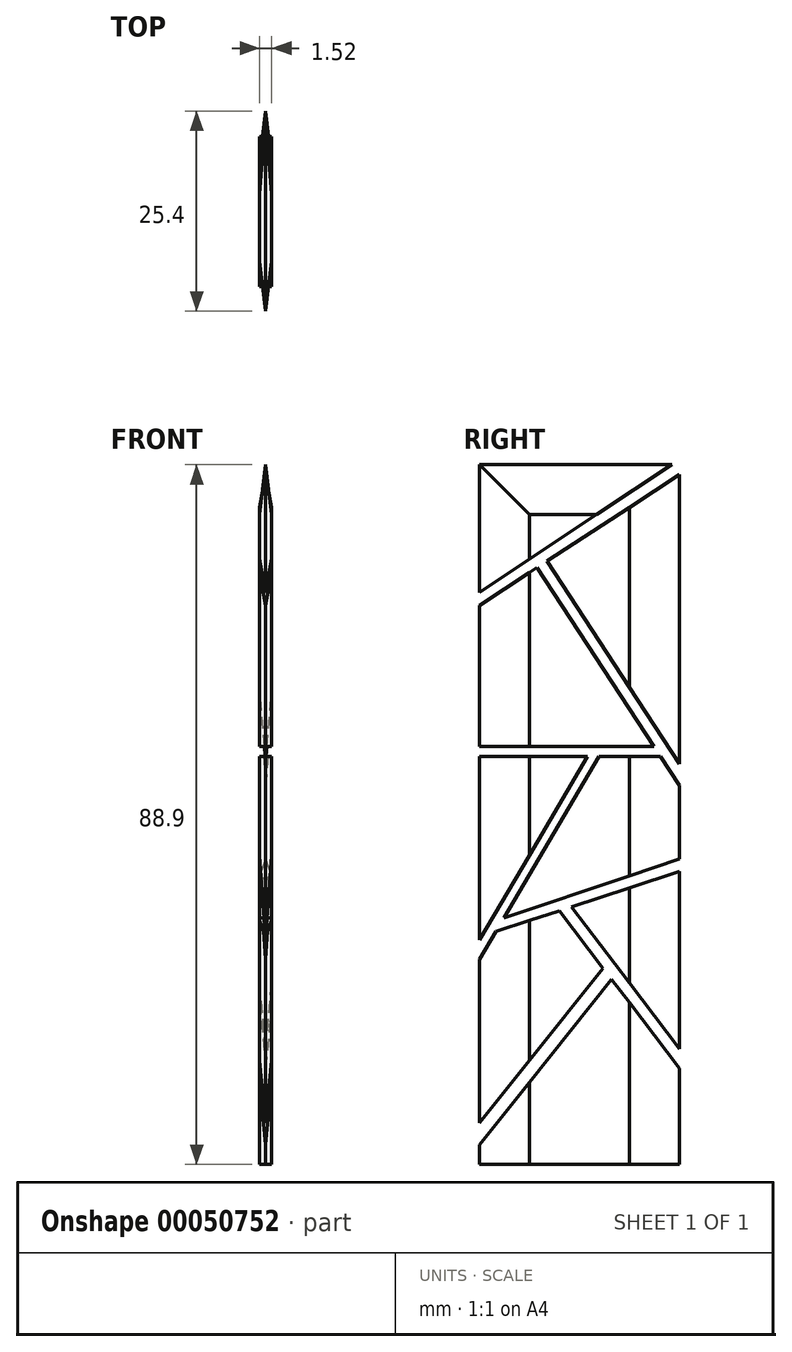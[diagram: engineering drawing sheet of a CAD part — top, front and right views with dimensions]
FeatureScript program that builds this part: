
annotation { "Feature Type Name" : "Feature", "Feature Type Description" : "" }
export const myFeature = defineFeature(function(context is Context, id is Id, definition is map)
    precondition{}
    {
        {
            var Q0;
            Q0=qCreatedBy(makeId("Right.planeOp"),FACE);
            var sketch = newSketch(context, id + "F0", { "sketchPlane" : qUnion([Q0])});
            skLineSegment(sketch, "E0", {"start": v(0, 0) * mm, "end": v(-12.7, 0) * mm});
            skLineSegment(sketch, "E1", {"start": v(-12.7, 0) * mm, "end": v(0, 0) * mm});
            skLineSegment(sketch, "E2", {"start": v(0, 0) * mm, "end": v(12.7, 0) * mm});
            skLineSegment(sketch, "E3", {"start": v(-12.7, 0) * mm, "end": v(-12.7, 51.83) * mm});
            skLineSegment(sketch, "E4", {"start": v(12.7, 0) * mm, "end": v(12.7, 88.9) * mm});
            skLineSegment(sketch, "E5", {"start": v(-12.7, 88.9) * mm, "end": v(11.76, 88.9) * mm});
            skLineSegment(sketch, "E6", {"start": v(11.76, 88.9) * mm, "end": v(-12.7, 72.67) * mm});
            skLineSegment(sketch, "E7", {"start": v(-12.7, 71.03) * mm, "end": v(-5.37, 75.82) * mm});
            skLineSegment(sketch, "E8.trimOffspring", {"start": v(-12.7, 72.67) * mm, "end": v(-12.7, 88.9) * mm});
            skLineSegment(sketch, "E9", {"start": v(-4.12, 76.63) * mm, "end": v(12.7, 50.88) * mm});
            skLineSegment(sketch, "E10", {"start": v(-5.37, 75.82) * mm, "end": v(9.49, 53.08) * mm});
            skLineSegment(sketch, "E11", {"start": v(9.49, 53.08) * mm, "end": v(-12.7, 53.08) * mm});
            skLineSegment(sketch, "E12", {"start": v(-12.7, 51.83) * mm, "end": v(1.05, 51.83) * mm});
            skLineSegment(sketch, "E13.trimOffspring", {"start": v(-12.7, 53.08) * mm, "end": v(-12.7, 71.03) * mm});
            skLineSegment(sketch, "E14.trimOffspring", {"start": v(10.3, 51.83) * mm, "end": v(12.7, 48.17) * mm});
            skLineSegment(sketch, "E15.trimOffspring", {"start": v(-4.12, 76.63) * mm, "end": v(12.7, 87.63) * mm});
            skLineSegment(sketch, "E16", {"start": v(2.51, 51.83) * mm, "end": v(-9.59, 31.31) * mm});
            skLineSegment(sketch, "E17", {"start": v(-12.7, 28.5) * mm, "end": v(1.05, 51.83) * mm});
            skPoint(sketch, "E18.start.orphan", {"position": v(0, 51.83) * mm});
            skLineSegment(sketch, "E19.trimOffspring", {"start": v(2.51, 51.83) * mm, "end": v(10.3, 51.83) * mm});
            skLineSegment(sketch, "E20", {"start": v(-10.6, 29.6) * mm, "end": v(-2.52, 32.23) * mm});
            skLineSegment(sketch, "E21", {"start": v(-9.59, 31.31) * mm, "end": v(12.7, 38.78) * mm});
            skLineSegment(sketch, "E22.trimOffspring", {"start": v(-10.6, 29.6) * mm, "end": v(-12.7, 26.03) * mm});
            skLineSegment(sketch, "E23", {"start": v(-2.52, 32.23) * mm, "end": v(3.03, 24.93) * mm});
            skLineSegment(sketch, "E24", {"start": v(-1.01, 32.73) * mm, "end": v(12.7, 14.67) * mm});
            skPoint(sketch, "E25.start.orphan", {"position": v(0, 33.05) * mm});
            skLineSegment(sketch, "E26", {"start": v(3.03, 24.93) * mm, "end": v(-12.7, 5.26) * mm});
            skLineSegment(sketch, "E27", {"start": v(4.1, 23.51) * mm, "end": v(-12.7, 2.5) * mm});
            skLineSegment(sketch, "E28.trimOffspring", {"start": v(-1.01, 32.73) * mm, "end": v(12.7, 37.2) * mm});
            skLineSegment(sketch, "E29.trimOffspring", {"start": v(4.1, 23.51) * mm, "end": v(12.7, 12.2) * mm});
            skSolve(sketch);
        }
        {
            var Q0;
            Q0 = qSketchRegion(id + "F0", true);
            extrude(context, id + "F1", {"entities" : qUnion([Q0]), "endBound" : BoundingType.SYMMETRIC, "depth" : 1.52 * mm});
        }
        {
            var Q0;
            {var subQ0=sQuery(id+"F0.wireOp",EDGE,"E4");Q0=makeQuery(id+"F1.opExtrude","CAP_EDGE",EDGE,{"disambiguationData":[OSD([subQ0]),TDD([makeQuery(id+"F0.imprint","IMPRINT",EDGE,{"disambiguationData":[TD([[makeQuery(id+"F0.imprint","INTERSECT",VERTEX,{"derivedFrom":[subQ0,sQuery(id+"F0.wireOp",EDGE,"E14.trimOffspring")]}),1.0]])],"derivedFrom":subQ0})])],"isStart":false});}
            var Q1;
            {var subQ0=sQuery(id+"F0.wireOp",EDGE,"E4");Q1=makeQuery(id+"F1.opExtrude","CAP_EDGE",EDGE,{"disambiguationData":[OSD([subQ0]),TDD([makeQuery(id+"F0.imprint","IMPRINT",EDGE,{"disambiguationData":[TD([[makeQuery(id+"F0.imprint","INTERSECT",VERTEX,{"derivedFrom":[subQ0,sQuery(id+"F0.wireOp",EDGE,"E14.trimOffspring")]}),1.0]])],"derivedFrom":subQ0})])],"isStart":true});}
            var Q2;
            {var subQ0=sQuery(id+"F0.wireOp",EDGE,"E4");Q2=makeQuery(id+"F1.opExtrude","CAP_EDGE",EDGE,{"disambiguationData":[OSD([subQ0]),TDD([makeQuery(id+"F0.imprint","IMPRINT",EDGE,{"disambiguationData":[TD([[makeQuery(id+"F0.imprint","INTERSECT",VERTEX,{"derivedFrom":[subQ0,sQuery(id+"F0.wireOp",EDGE,"E9")]}),-1.0]])],"derivedFrom":subQ0})])],"isStart":false});}
            var Q3;
            {var subQ0=sQuery(id+"F0.wireOp",EDGE,"E4");Q3=makeQuery(id+"F1.opExtrude","CAP_EDGE",EDGE,{"disambiguationData":[OSD([subQ0]),TDD([makeQuery(id+"F0.imprint","IMPRINT",EDGE,{"disambiguationData":[TD([[makeQuery(id+"F0.imprint","INTERSECT",VERTEX,{"derivedFrom":[subQ0,sQuery(id+"F0.wireOp",EDGE,"E24")]}),-1.0]])],"derivedFrom":subQ0})])],"isStart":false});}
            var Q4;
            {var subQ0=sQuery(id+"F0.wireOp",EDGE,"E4");Q4=makeQuery(id+"F1.opExtrude","CAP_EDGE",EDGE,{"disambiguationData":[OSD([subQ0]),TDD([makeQuery(id+"F0.imprint","IMPRINT",EDGE,{"disambiguationData":[TD([[makeQuery(id+"F0.imprint","INTERSECT",VERTEX,{"derivedFrom":[sQuery(id+"F0.wireOp",EDGE,"E2"),subQ0]}),-1.0]])],"derivedFrom":subQ0})])],"isStart":false});}
            var Q5;
            Q5=makeQuery(id+"F1.opExtrude","CAP_EDGE",EDGE,{"disambiguationData":[OSD([sQuery(id+"F0.wireOp",EDGE,"E8.trimOffspring")])],"isStart":true});
            var Q6;
            Q6=makeQuery(id+"F1.opExtrude","CAP_EDGE",EDGE,{"disambiguationData":[OSD([sQuery(id+"F0.wireOp",EDGE,"E13.trimOffspring")])],"isStart":true});
            var Q7;
            {var subQ0=sQuery(id+"F0.wireOp",EDGE,"E3");Q7=makeQuery(id+"F1.opExtrude","CAP_EDGE",EDGE,{"disambiguationData":[OSD([subQ0]),TDD([makeQuery(id+"F0.imprint","IMPRINT",EDGE,{"disambiguationData":[TD([[makeQuery(id+"F0.imprint","INTERSECT",VERTEX,{"derivedFrom":[subQ0,sQuery(id+"F0.wireOp",EDGE,"E12")]}),1.0]])],"derivedFrom":subQ0})])],"isStart":true});}
            var Q8;
            {var subQ0=sQuery(id+"F0.wireOp",EDGE,"E3");Q8=makeQuery(id+"F1.opExtrude","CAP_EDGE",EDGE,{"disambiguationData":[OSD([subQ0]),TDD([makeQuery(id+"F0.imprint","IMPRINT",EDGE,{"disambiguationData":[TD([[makeQuery(id+"F0.imprint","INTERSECT",VERTEX,{"derivedFrom":[subQ0,sQuery(id+"F0.wireOp",EDGE,"E22.trimOffspring")]}),1.0]])],"derivedFrom":subQ0})])],"isStart":true});}
            var Q9;
            {var subQ0=sQuery(id+"F0.wireOp",EDGE,"E3");Q9=makeQuery(id+"F1.opExtrude","CAP_EDGE",EDGE,{"disambiguationData":[OSD([subQ0]),TDD([makeQuery(id+"F0.imprint","IMPRINT",EDGE,{"disambiguationData":[TD([[makeQuery(id+"F0.imprint","INTERSECT",VERTEX,{"derivedFrom":[sQuery(id+"F0.wireOp",EDGE,"E1"),subQ0]}),-1.0]])],"derivedFrom":subQ0})])],"isStart":true});}
            var Q10;
            {var subQ0=sQuery(id+"F0.wireOp",EDGE,"E3");Q10=makeQuery(id+"F1.opExtrude","CAP_EDGE",EDGE,{"disambiguationData":[OSD([subQ0]),TDD([makeQuery(id+"F0.imprint","IMPRINT",EDGE,{"disambiguationData":[TD([[makeQuery(id+"F0.imprint","INTERSECT",VERTEX,{"derivedFrom":[sQuery(id+"F0.wireOp",EDGE,"E1"),subQ0]}),-1.0]])],"derivedFrom":subQ0})])],"isStart":false});}
            var Q11;
            {var subQ0=sQuery(id+"F0.wireOp",EDGE,"E3");Q11=makeQuery(id+"F1.opExtrude","CAP_EDGE",EDGE,{"disambiguationData":[OSD([subQ0]),TDD([makeQuery(id+"F0.imprint","IMPRINT",EDGE,{"disambiguationData":[TD([[makeQuery(id+"F0.imprint","INTERSECT",VERTEX,{"derivedFrom":[subQ0,sQuery(id+"F0.wireOp",EDGE,"E22.trimOffspring")]}),1.0]])],"derivedFrom":subQ0})])],"isStart":false});}
            var Q12;
            {var subQ0=sQuery(id+"F0.wireOp",EDGE,"E3");Q12=makeQuery(id+"F1.opExtrude","CAP_EDGE",EDGE,{"disambiguationData":[OSD([subQ0]),TDD([makeQuery(id+"F0.imprint","IMPRINT",EDGE,{"disambiguationData":[TD([[makeQuery(id+"F0.imprint","INTERSECT",VERTEX,{"derivedFrom":[subQ0,sQuery(id+"F0.wireOp",EDGE,"E12")]}),1.0]])],"derivedFrom":subQ0})])],"isStart":false});}
            var Q13;
            Q13=makeQuery(id+"F1.opExtrude","CAP_EDGE",EDGE,{"disambiguationData":[OSD([sQuery(id+"F0.wireOp",EDGE,"E13.trimOffspring")])],"isStart":false});
            var Q14;
            Q14=makeQuery(id+"F1.opExtrude","CAP_EDGE",EDGE,{"disambiguationData":[OSD([sQuery(id+"F0.wireOp",EDGE,"E8.trimOffspring")])],"isStart":false});
            var Q15;
            Q15=makeQuery(id+"F1.opExtrude","CAP_EDGE",EDGE,{"disambiguationData":[OSD([sQuery(id+"F0.wireOp",EDGE,"E5")])],"isStart":true});
            var Q16;
            {var subQ0=sQuery(id+"F0.wireOp",EDGE,"E4");Q16=makeQuery(id+"F1.opExtrude","CAP_EDGE",EDGE,{"disambiguationData":[OSD([subQ0]),TDD([makeQuery(id+"F0.imprint","IMPRINT",EDGE,{"disambiguationData":[TD([[makeQuery(id+"F0.imprint","INTERSECT",VERTEX,{"derivedFrom":[subQ0,sQuery(id+"F0.wireOp",EDGE,"E9")]}),-1.0]])],"derivedFrom":subQ0})])],"isStart":true});}
            var Q17;
            {var subQ0=sQuery(id+"F0.wireOp",EDGE,"E4");Q17=makeQuery(id+"F1.opExtrude","CAP_EDGE",EDGE,{"disambiguationData":[OSD([subQ0]),TDD([makeQuery(id+"F0.imprint","IMPRINT",EDGE,{"disambiguationData":[TD([[makeQuery(id+"F0.imprint","INTERSECT",VERTEX,{"derivedFrom":[subQ0,sQuery(id+"F0.wireOp",EDGE,"E24")]}),-1.0]])],"derivedFrom":subQ0})])],"isStart":true});}
            var Q18;
            {var subQ0=sQuery(id+"F0.wireOp",EDGE,"E4");Q18=makeQuery(id+"F1.opExtrude","CAP_EDGE",EDGE,{"disambiguationData":[OSD([subQ0]),TDD([makeQuery(id+"F0.imprint","IMPRINT",EDGE,{"disambiguationData":[TD([[makeQuery(id+"F0.imprint","INTERSECT",VERTEX,{"derivedFrom":[sQuery(id+"F0.wireOp",EDGE,"E2"),subQ0]}),-1.0]])],"derivedFrom":subQ0})])],"isStart":true});}
            chamfer(context, id + "F2", {"entities" : qUnion([Q0, Q1, Q2, Q3, Q4, Q5, Q6, Q7, Q8, Q9, Q10, Q11, Q12, Q13, Q14, Q15, Q16, Q17, Q18]), "chamferType" : ChamferType.TWO_OFFSETS, "width1" : 6.35 * mm, "oppositeDirection" : false, "width2" : 0.76 * mm, "tangentPropagation" : true});
        }
        {
            var Q0;
            Q0=makeQuery(id+"F1.opExtrude","CAP_EDGE",EDGE,{"disambiguationData":[OSD([sQuery(id+"F0.wireOp",EDGE,"E5")])],"isStart":false});
            chamfer(context, id + "F3", {"entities" : qUnion([Q0]), "chamferType" : ChamferType.TWO_OFFSETS, "width1" : 0.76 * mm, "oppositeDirection" : false, "width2" : 6.35 * mm, "tangentPropagation" : true});
        }
    });
